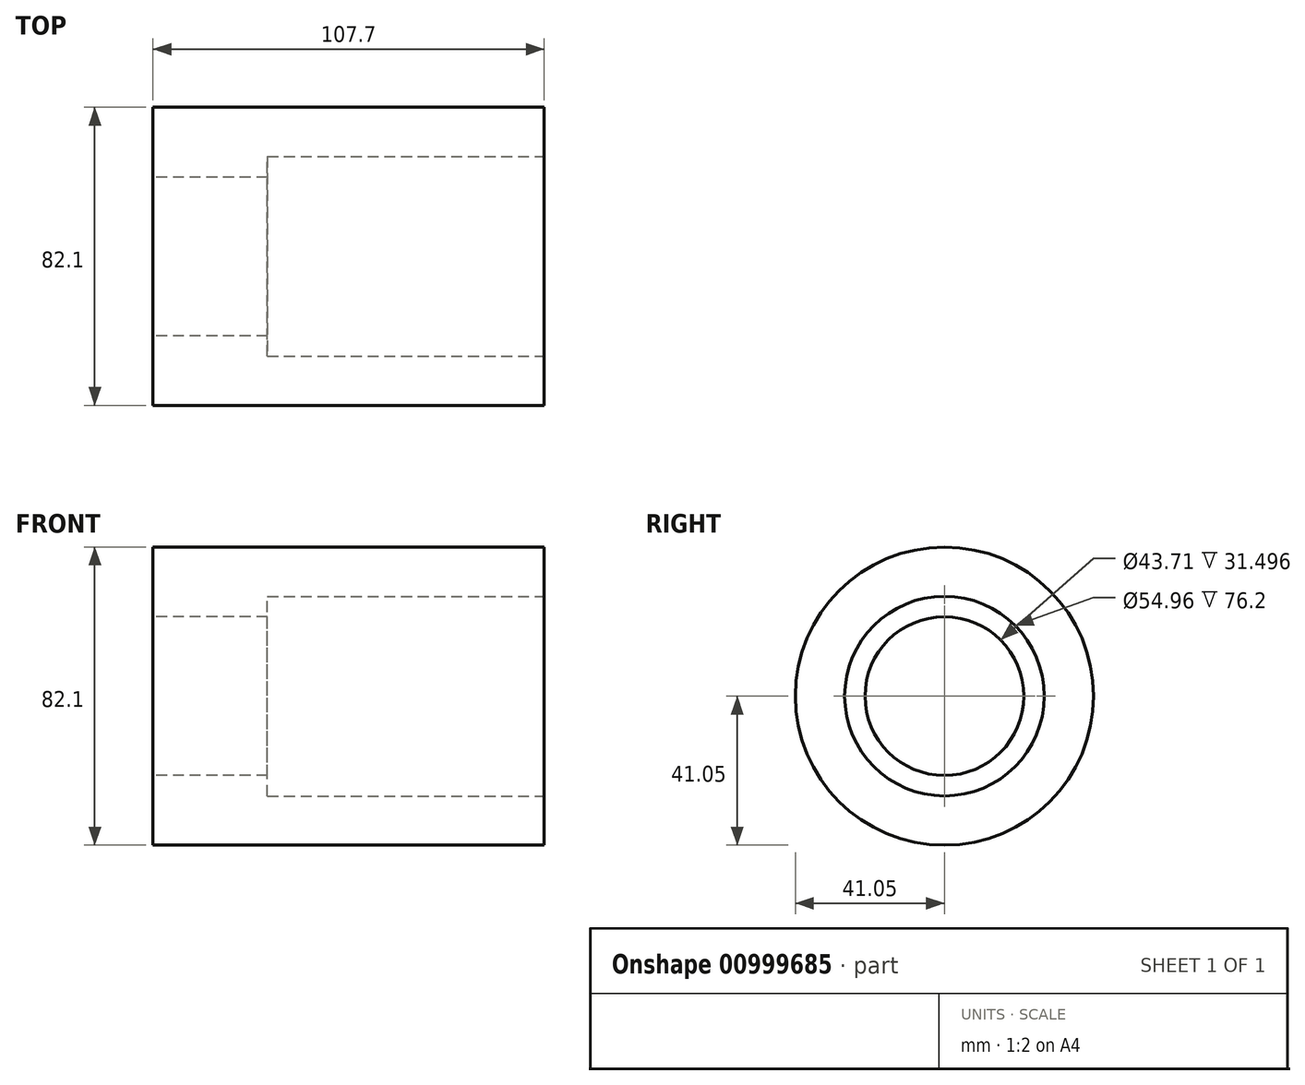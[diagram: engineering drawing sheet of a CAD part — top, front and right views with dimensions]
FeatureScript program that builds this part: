
annotation { "Feature Type Name" : "Feature", "Feature Type Description" : "" }
export const myFeature = defineFeature(function(context is Context, id is Id, definition is map)
    precondition{}
    {
        {
            var Q0;
            Q0=qCreatedBy(makeId("Right.planeOp"),FACE);
            var sketch = newSketch(context, id + "F0", { "sketchPlane" : qUnion([Q0])});
            skCircle(sketch, "E0", {"center": v(0, 0) * mm, "radius": 41.05 * mm});
            skSolve(sketch);
        }
        {
            var Q0;
            Q0=makeQuery(id+"F0.imprint","IMPRINT",FACE,{"disambiguationData":[TD([[makeQuery(id+"F0.imprint","IMPRINT",EDGE,{"derivedFrom":sQuery(id+"F0.wireOp",EDGE,"E0")}),1.0]])]});
            extrude(context, id + "F1", {"entities" : qUnion([Q0]), "depth" : 107.7 * mm, "offsetDistance" : 25.4 * mm});
        }
        {
            var Q0;
            Q0=makeQuery(id+"F1.opExtrude","CAP_FACE",FACE,{"disambiguationData":[OSD([sQuery(id+"F0.wireOp",EDGE,"E0")])],"isStart":true});
            var sketch = newSketch(context, id + "F2", { "sketchPlane" : qUnion([Q0])});
            skCircle(sketch, "E1", {"center": v(0, 0) * mm, "radius": 21.85 * mm});
            skSolve(sketch);
        }
        {
            var Q0;
            Q0=makeQuery(id+"F2.imprint","IMPRINT",FACE,{"disambiguationData":[TD([[makeQuery(id+"F2.imprint","IMPRINT",EDGE,{"derivedFrom":sQuery(id+"F2.wireOp",EDGE,"E1")}),1.0]])]});
            var Q1;
            Q1=sQuery(id+"F2.wireOp",EDGE,"E1");
            extrude(context, id + "F3", {"entities" : qUnion([Q0]), "operationType" : NewBodyOperationType.REMOVE, "surfaceEntities" : qUnion([Q1]), "oppositeDirection" : true, "depth" : 236.47 * mm, "offsetDistance" : 25.4 * mm});
        }
        {
            var Q0;
            Q0=makeQuery(id+"F1.opExtrude","CAP_FACE",FACE,{"disambiguationData":[OSD([sQuery(id+"F0.wireOp",EDGE,"E0")])],"isStart":false});
            var sketch = newSketch(context, id + "F4", { "sketchPlane" : qUnion([Q0])});
            skCircle(sketch, "E2", {"center": v(0, 0) * mm, "radius": 27.48 * mm});
            skSolve(sketch);
        }
        {
            var Q0;
            Q0=makeQuery(id+"F4.imprint","IMPRINT",FACE,{"disambiguationData":[TD([[makeQuery(id+"F4.imprint","IMPRINT",EDGE,{"derivedFrom":sQuery(id+"F4.wireOp",EDGE,"E2")}),1.0]])]});
            var sketch = newSketch(context, id + "F5", { "sketchPlane" : qUnion([Q0])});
            skSolve(sketch);
        }
        {
            var Q0;
            Q0=makeQuery(id+"F5.imprint","IMPRINT",FACE,{"disambiguationData":[TD([[makeQuery(id+"F5.imprint","IMPRINT",EDGE,{"derivedFrom":makeQuery(id+"F4.imprint","IMPRINT",EDGE,{"derivedFrom":sQuery(id+"F4.wireOp",EDGE,"E2")})}),1.0]])]});
            var Q1;
            Q1=makeQuery(id+"F4.imprint","IMPRINT",FACE,{"disambiguationData":[TD([[makeQuery(id+"F4.imprint","IMPRINT",EDGE,{"derivedFrom":sQuery(id+"F4.wireOp",EDGE,"E2")}),1.0]])]});
            extrude(context, id + "F6", {"entities" : qUnion([Q0, Q1]), "operationType" : NewBodyOperationType.REMOVE, "oppositeDirection" : true, "depth" : 76.2 * mm, "offsetDistance" : 25.4 * mm});
        }
    });
